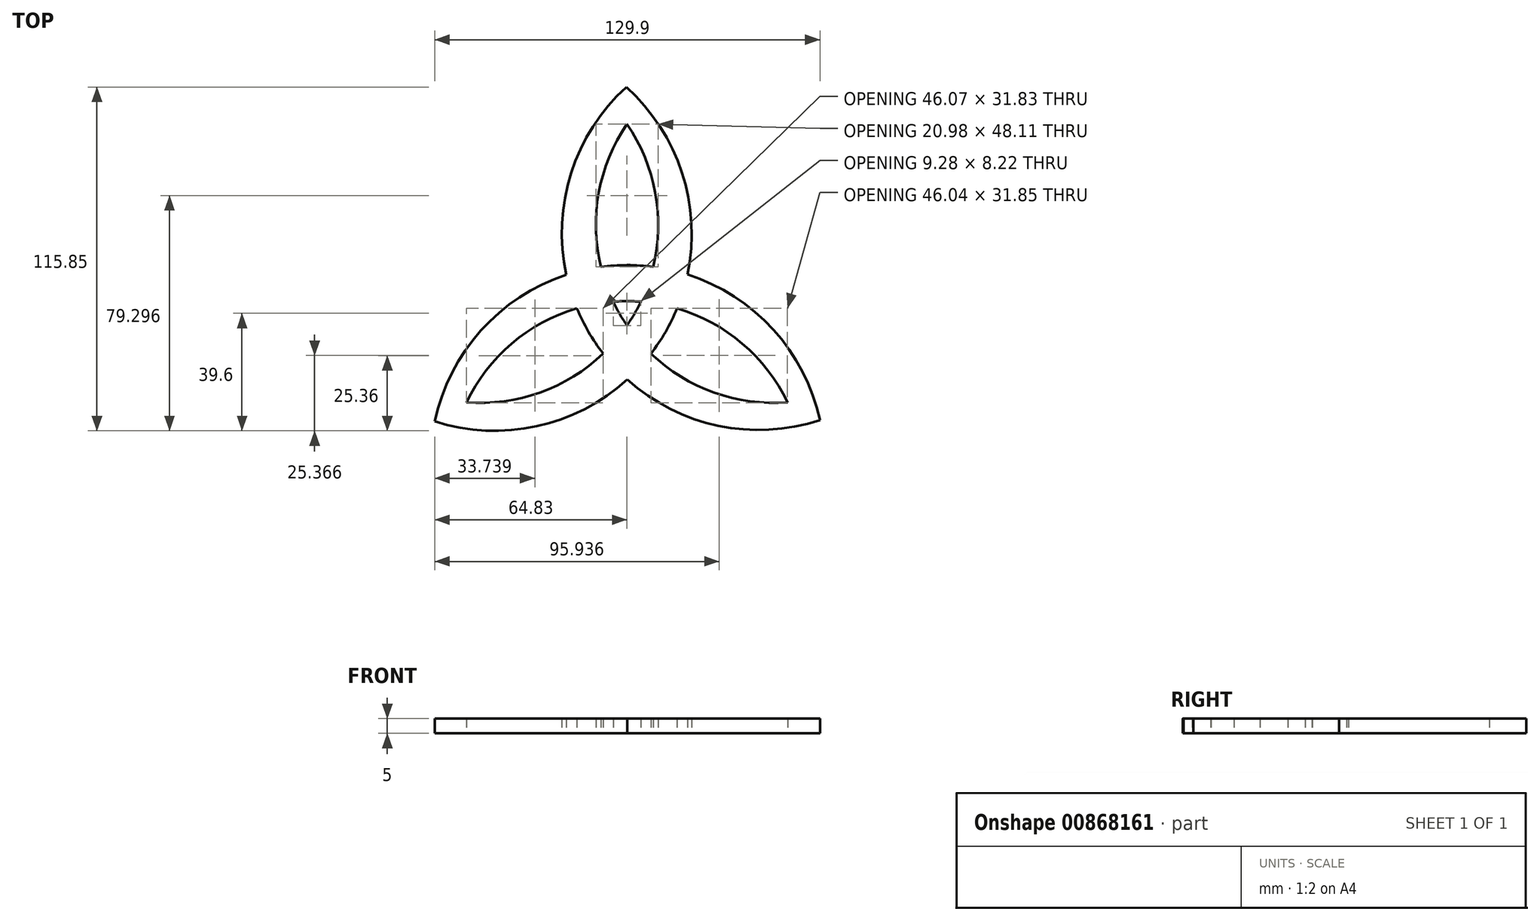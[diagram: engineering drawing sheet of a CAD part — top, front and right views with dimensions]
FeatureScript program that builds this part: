
annotation { "Feature Type Name" : "Feature", "Feature Type Description" : "" }
export const myFeature = defineFeature(function(context is Context, id is Id, definition is map)
    precondition{}
    {
        {
            var Q0;
            Q0=qCreatedBy(makeId("Top.planeOp"),FACE);
            var sketch = newSketch(context, id + "F0", { "sketchPlane" : qUnion([Q0])});
            skCircle(sketch, "E0", {"center": v(0, 0) * mm, "radius": 75 * mm});
            skCircle(sketch, "E1.cCircle", {"center": v(0, 0) * mm, "radius": 75 * mm, "construction": true});
            skArc(sketch, "E2", {"start": v(65.07, -37.3) * mm, "mid": v(49.3, -6.74) * mm, "end": v(20.38, 11.85) * mm});
            skArc(sketch, "E3", {"start": v(-64.83, -37.7) * mm, "mid": v(-30.49, -39.33) * mm, "end": v(0.07, -23.57) * mm});
            skArc(sketch, "E4", {"start": v(-0.23, 75) * mm, "mid": v(-18.82, 46.07) * mm, "end": v(-20.45, 11.72) * mm});
            skArc(sketch, "E5", {"start": v(-54.13, -31.25) * mm, "mid": v(-29.34, -27.95) * mm, "end": v(-8.06, -14.83) * mm});
            skArc(sketch, "E6", {"start": v(54.13, -31.25) * mm, "mid": v(38.87, -11.44) * mm, "end": v(16.87, 0.44) * mm});
            skArc(sketch, "E7", {"start": v(0, 62.5) * mm, "mid": v(-9.53, 39.38) * mm, "end": v(-8.82, 14.4) * mm});
            skArc(sketch, "E8.trimOffspring", {"start": v(-16.91, 0.43) * mm, "mid": v(16.69, -34.5) * mm, "end": v(65.07, -37.3) * mm});
            skArc(sketch, "E9.trimOffspring", {"start": v(-4.64, 2.68) * mm, "mid": v(19.49, -23.4) * mm, "end": v(54.13, -31.25) * mm});
            skArc(sketch, "E10.trimOffspring", {"start": v(8.83, 14.43) * mm, "mid": v(-38.22, 2.8) * mm, "end": v(-64.83, -37.7) * mm});
            skArc(sketch, "E11.trimOffspring", {"start": v(4.64, 2.68) * mm, "mid": v(-30, -5.18) * mm, "end": v(-54.13, -31.25) * mm});
            skArc(sketch, "E12.trimOffspring", {"start": v(8.09, -14.86) * mm, "mid": v(21.53, 31.7) * mm, "end": v(-0.23, 75) * mm});
            skArc(sketch, "E13.trimOffspring", {"start": v(0, -5.36) * mm, "mid": v(10.51, 28.57) * mm, "end": v(0, 62.5) * mm});
            skSolve(sketch);
        }
        {
            var Q0;
            {var subQ4=sQuery(id+"F0.wireOp",EDGE,"E3");Q0=makeQuery(id+"F0.imprint","IMPRINT",FACE,{"disambiguationData":[TD([[makeQuery(id+"F0.imprint","IMPRINT",EDGE,{"derivedFrom":subQ4}),1.0]])]});}
            var Q1;
            {var subQ1=sQuery(id+"F0.wireOp",EDGE,"E4");Q1=makeQuery(id+"F0.imprint","IMPRINT",FACE,{"disambiguationData":[TD([[makeQuery(id+"F0.imprint","IMPRINT",EDGE,{"derivedFrom":subQ1}),1.0]])]});}
            var Q2;
            {var subQ6=sQuery(id+"F0.wireOp",EDGE,"E2");Q2=makeQuery(id+"F0.imprint","IMPRINT",FACE,{"disambiguationData":[TD([[makeQuery(id+"F0.imprint","IMPRINT",EDGE,{"derivedFrom":subQ6}),1.0]])]});}
            extrude(context, id + "F1", {"entities" : qUnion([Q0, Q1, Q2]), "depth" : 5 * mm, "offsetDistance" : 25 * mm});
        }
    });
